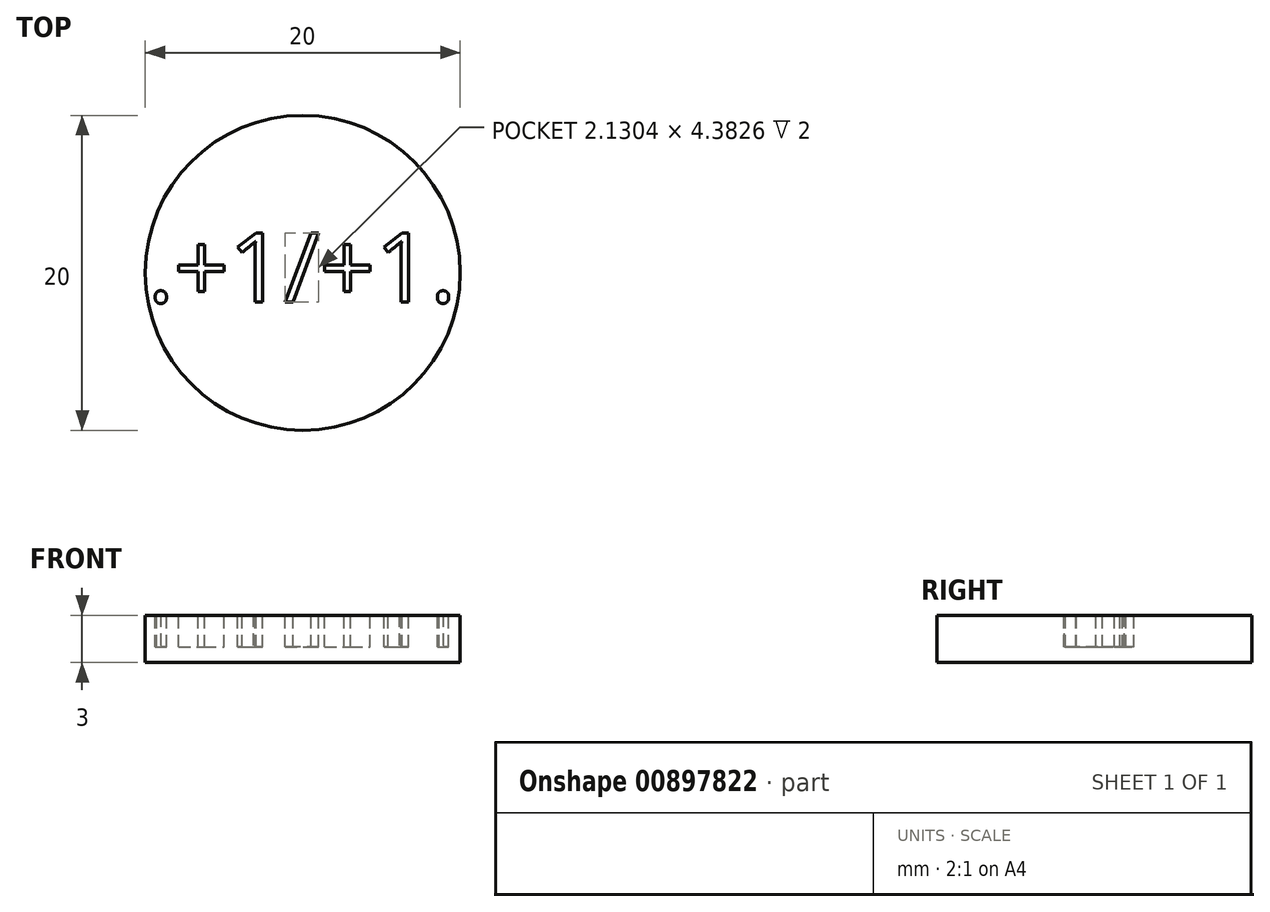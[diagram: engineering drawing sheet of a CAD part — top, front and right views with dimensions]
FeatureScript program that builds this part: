
annotation { "Feature Type Name" : "Feature", "Feature Type Description" : "" }
export const myFeature = defineFeature(function(context is Context, id is Id, definition is map)
    precondition{}
    {
        {
            var Q0;
            Q0=qCreatedBy(makeId("Top.planeOp"),FACE);
            var sketch = newSketch(context, id + "F0", { "sketchPlane" : qUnion([Q0])});
            skCircle(sketch, "E0", {"center": v(0, 0) * mm, "radius": 10 * mm});
            skSolve(sketch);
        }
        {
            var Q0;
            Q0=makeQuery(id+"F0.imprint","IMPRINT",FACE,{"disambiguationData":[TD([[makeQuery(id+"F0.imprint","IMPRINT",EDGE,{"derivedFrom":sQuery(id+"F0.wireOp",EDGE,"E0")}),1.0]])]});
            extrude(context, id + "F1", {"entities" : qUnion([Q0]), "depth" : 3 * mm, "offsetDistance" : 25 * mm});
        }
        {
            var Q0;
            Q0=makeQuery(id+"F1.opExtrude","CAP_FACE",FACE,{"disambiguationData":[OSD([sQuery(id+"F0.wireOp",EDGE,"E0")])],"isStart":false});
            var sketch = newSketch(context, id + "F2", { "sketchPlane" : qUnion([Q0])});
            skText(sketch, "E1", { "text": ".+1/+1.", "fontName": "OpenSans-Regular.ttf"});
            const initialGuessF2  = {"E1": [-0.00983, -0.00186, 1, 0, 0.00442]};
            skSetInitialGuess(sketch, initialGuessF2);
            skSolve(sketch);
        }
        {
            var Q0;
            Q0 = qSketchRegion(id + "F2", true);
            extrude(context, id + "F3", {"entities" : qUnion([Q0]), "operationType" : NewBodyOperationType.REMOVE, "oppositeDirection" : true, "depth" : 2 * mm, "offsetDistance" : 25 * mm});
        }
    });
